# Revit family: 65232213
name_source: partatom
category: Plumbing Fixtures
revit_build: Autodesk Revit 2018 (Build: 20170223_1515(x64)
units: mm (PartAtom-declared; Revit-internal decimal feet)

## family parameters
Always vertical = Yes
Cut with Voids When Loaded = No
OmniClass Number = 23.45.55.00
OmniClass Title = Sanitary Faucets, Wastes
Part Type = Normal
Room Calculation Point = No
Round Connector Dimension = Use Diameter
Shared = No
Work Plane-Based = No

## types (1)
- 65232213 Kitchen faucet, 230/5 V
    2D/3D/BIM Files URL = http://static.hansa.com
    3D View = https://static.hansa.com
    Additional Features = Faucet is GGT-approved user test VERY GOOD
    Advanced Features = Surfaces in contact with drinking water contain less than 0.3% lead;Inner body made of DZR brass;Waterways without nickel coating;Software settings adjustable via buttons
    Aerator = Hidden aerator;Standard aerator
    Afterflow Period = 4 s (2/4/8/10/20 s)
    Ambience photo = http://static.hansa.com
    AssetType = Fixed
    Automatic Flush Frequency = off (off/12/24/48/72 h)
    Automatic Flush Period = 30 s (10/30/60/120/180 s)
    BIMObjectName = 65232213
    Backflow Prevention EN1717 = AA
    BodyMaterial = Brass
    Brand = HANSA
    Catalog Drawing URL = http://static.hansa.com
    Category = Kitchen
    CloseOffRating = 0
    Color = Chrome
    Connection = Flexible inlet pipes
    Connection Size = G3/8
    Dimension Drawing URL = http://static.hansa.com
    DurationUnit = Year
    EAN Number = 4015474273443
    EMC Directive = 2014/30/EU , 2014/35/EU , 2011/65/EU
    ETIM Class Number = EC011431 Kitchen mixing tap
    Electrical Connection = 230 / 5 V
    Electronic Parts = Autofocus infrared sensor;Solenoid valve;External control unit;Power supply;Light indicated function(s)
    FDV Document URL = http://www.hansa.com
    FaucetMainMaterial = Brass
    Features = Hybrid;Plug transformer
    Finish = Polished
    Flow Drawing URL = http://static.hansa.com
    Flow Rate At 300kPa = 0.2 L/s
    FlowCoefficient = 0
    Group = Kitchen faucet
    IfcExportAs = IfcValveType
    IfcExportType = FAUCET
    InletConnectionSize = 10 mm  [stored 0.0328084 ft]
    Installation Type = Deck mounted
    Installation and Maintenance Guide URL = http://static.hansa.com
    Interactive AR View URL = https://static.hansa.com
    Lever Handle = Two operating levers/handles;Easy-Grip surface
    Lifestyle photo = http://static.hansa.com
    Manufacturer = HANSA
    ManufacturerName = HANSA
    ManufacturerURL = http://www.hansa.com
    Market = Austria;Belgium;Czech Republic;Germany;Spain;France;International;Italy;Netherlands;Slovakia
    Material = Brass
    Max Flow Period = 40 s (10/40/60/120/180 s)
    Max. Hot Water Supply = 70 °C
    Mechanical Parts = Ceramic head part for flow control;Mixing valve for manual temperature control;Litter filter(s)
    Mobile Product Information URL = http://mpi.hansa.com
    Model = 65232213 Kitchen faucet, 230/5 V
    ModelReference = 65232213
    Mounting Holes = 1 hole
    NBSDescription = Water supply fittings for wash basins and troughs
    NBSReference = 45-35-70/371
    Name = 65232213 Kitchen faucet, 230/5 V
    Name_en = 65232213 Kitchen faucet, 230/5 V
    Noise Class = I (ISO 3822)
    NominalDepth = 256 mm
    NominalHeight = 294 mm  [stored 0.964567 ft]
    NominalWidth = 122 mm  [stored 0.400262 ft]
    Operating Distance = 0-40 mm
    Operating Voltage = 5 V
    Pressure Loss With Flow 02ls = 290000.0 Pa
    Product Code = 65232213
    Product Family = HANSAFIT Hybrid
    Product Image URL = http://static.hansa.com
    Product URL = http://static.hansa.com
    ProductInformation = Kitchen faucet with an easy-grip lever, high swivel spout and aerator.
    Protection Class = IP 54 / transformer IP 20
    Revision = 4
    Sales Package dimensions (LxWxH) = 460 x 300 x 130
    Shape = Sculptured
    Size = 120x255x300 mm
    Spare-Part Information URL = http://static.hansa.com
    Spout Projection = 193 mm
    Spout Swivel Range = 120° (80° / 60°)
    Spout Type = Swivel spout;Swivel range limiting option
    Surface treatment = Chrome
    Technical DataSheet URL = http://www.hansa.com
    UNSPSC Class Number = 30181700 Faucets or taps
    URL Declaration of Conformity = http://static.hansa.com
    URL REACH = http://static.hansa.com
    URL WEEE = http://www.hansa.com
    Uniclass2 = Pr_40_30_96_96
    Uniclass2015Description = Washbasin manual water supply sets
    Uniclass2015Reference = Pr_40_20_87_96
    Version = 4
    VersionDate = 01/07/2022
    Warranty Information URL = http://warranty.hansa.com
    WarrantyDescription = http://warranty.hansa.com
    WarrantyDurationUnit = Year
    Working Pressure = 100 - 1000 kPa
    WorkingPressure = 100 - 1000 kPa

note: [stored X ft] marks values corroborated as IEEE doubles in the binary element streams (Revit-internal decimal feet)

## geometry (parser evidence)
native form markers: Sweep x6
no freeform markers — native parametric forms only
